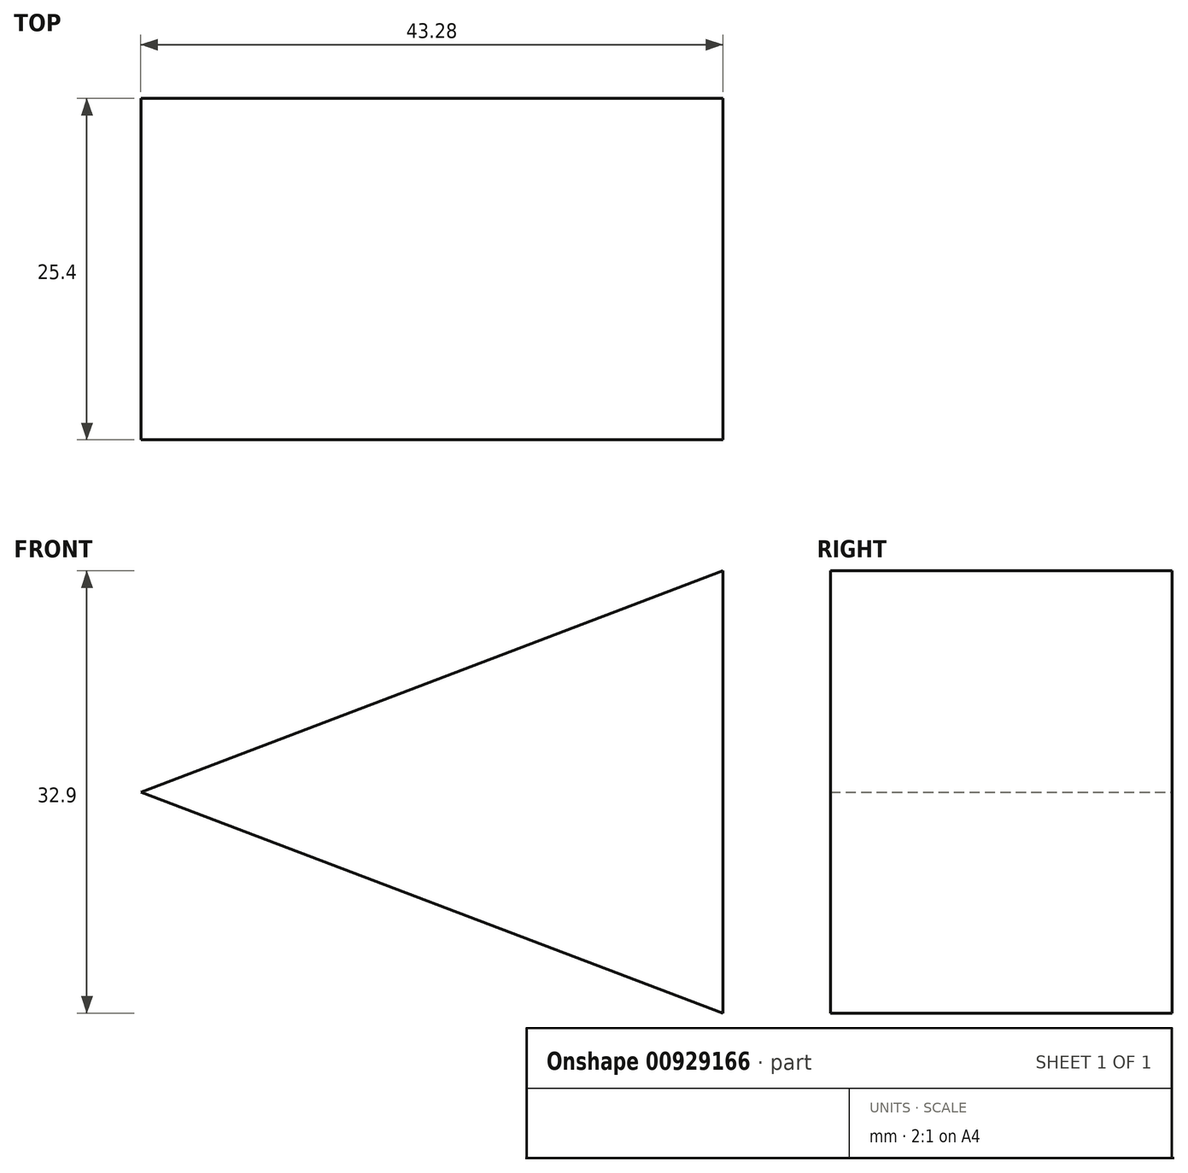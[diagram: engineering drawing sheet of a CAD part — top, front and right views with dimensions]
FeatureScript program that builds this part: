
annotation { "Feature Type Name" : "Feature", "Feature Type Description" : "" }
export const myFeature = defineFeature(function(context is Context, id is Id, definition is map)
    precondition{}
    {
        {
            var Q0;
            Q0=qCreatedBy(makeId("Front.planeOp"),FACE);
            var sketch = newSketch(context, id + "F0", { "sketchPlane" : qUnion([Q0])});
            skLineSegment(sketch, "E0", {"start": v(0, 0) * mm, "end": v(0, 16.45) * mm});
            skLineSegment(sketch, "E1", {"start": v(0, 16.45) * mm, "end": v(-43.28, 0) * mm});
            skLineSegment(sketch, "E2", {"start": v(-43.28, 0) * mm, "end": v(0, 0) * mm});
            skSolve(sketch);
        }
        {
            var Q0;
            Q0=makeQuery(id+"F0.imprint","IMPRINT",FACE,{"disambiguationData":[TD([[makeQuery(id+"F0.imprint","IMPRINT",EDGE,{"derivedFrom":sQuery(id+"F0.wireOp",EDGE,"E0")}),1.0]])]});
            extrude(context, id + "F1", {"entities" : qUnion([Q0]), "depth" : 25.4 * mm, "offsetDistance" : 25.4 * mm});
        }
        {
            var Q0;
            Q0=makeQuery(id+"F1.opExtrude","SWEPT_BODY",BODY,{"disambiguationData":[OSD([sQuery(id+"F0.wireOp",EDGE,"E0"),sQuery(id+"F0.wireOp",EDGE,"E1"),sQuery(id+"F0.wireOp",EDGE,"E2")])]});
            var Q1;
            Q1=qCreatedBy(makeId("Top.planeOp"),FACE);
            mirror(context, id + "F2", {"operationType" : NewBodyOperationType.ADD, "entities" : qUnion([Q0]), "mirrorPlane" : qUnion([Q1])});
        }
    });
